# Revit family: LWplc_Latchwaysplc_BaluAndGuardSym_VersiRail_Ancillary
name_source: partatom
category: Railings
revit_build: Autodesk Revit 2013 (Build: 20121003_2115(x64)
units: mm (PartAtom-declared; Revit-internal decimal feet)

## types (5) — shared parameters
AssetType = Fixed
Description = Latchways ManSafe® for Roofing, using VersiRail
Diameter = 40 mm  [stored 0.131234 ft]
DurationUnit = year
GateMaterial = LWplc_Latchwaysplc_Aluminium_Polished
Height = 1100 mm
IfcExportAs = GUARDRAIL
IfcExportType = IfcRailing
IsExternal = Yes
ManufacturerName = Latchways plc
ManufacturerURL = www.latchways.com
Material = Handrails & Uprights: Aluminium
NBSDescription = Balustrade and guarding system
NBSReference = 25-25-10/110
NominalLength = 40 mm  [stored 0.131234 ft]
RailMaterial = LWplc_Latchwaysplc_Aluminium_Polished
SupportMaterial = LWplc_Latchwaysplc_Aluminium_Polished
URL = www.latchways.com
Uniclass2 = Ss_25_15_60_05
Version = 1
WarrantyDurationUnit = year
zero-valued in all types: Default Elevation

## per-type parameters (varying)
| type | 90DegreeCorner | AccessGate | BIMObjectName | ClosureEnd | HandRail | Model | ModelNumber | ModelReference | NominalHeight | NominalWidth | ProductInformation | Size | WallEndPiece |
| BalustradeAndGuardingSystem_VersiRailAncillary_90DegreeCorner_Latchwaysplc | Yes | No | LWplc_Latchwaysplc_BalustradeAndGuardingSystem_VersiRailAncillary_90DegreeCorner | No | No | 22061-00 | 22061-00 | VersiRail - Ancillary Items - 90 Degree Corner | 40 mm  [stored 0.131234 ft] | 160 mm  [stored 0.524934 ft] | www.latchways.com/BIM/Latchways_VersiRail_90DegreeCorner.pdf | 160 x 40 x 40 mm | No |
| BalustradeAndGuardingSystem_VersiRailAncillary_AccessGate_Latchwaysplc | No | Yes | LWplc_Latchwaysplc_BalustradeAndGuardingSystem_VersiRailAncillary_AccessGate | No | No | 22010-00 | 22010-00 | VersiRail - Ancillary Items - Access Gate | 510 mm  [stored 1.67323 ft] | 1160 mm  [stored 3.80577 ft] | www.latchways.com/BIM/Latchways_VersiRail_AccessGate.pdf | 1160 x 40 x 510 mm | No |
| BalustradeAndGuardingSystem_VersiRailAncillary_ClosureEnd_Latchwaysplc | No | No | LWplc_Latchwaysplc_BalustradeAndGuardingSystem_VersiRailAncillary_ClosureEnd | Yes | No | 22059-00 | 22059-00 | VersiRail - Ancillary Items - Closure End | 510 mm  [stored 1.67323 ft] | 160 mm  [stored 0.524934 ft] | www.latchways.com/BIM/Latchways_VersiRail_ClosureEndAssembly.pdf | 160 x 40 x 510 mm | No |
| BalustradeAndGuardingSystem_VersiRailAncillary_HandAndKneeRail_Latchwaysplc | No | No | LWplc_Latchwaysplc_BalustradeAndGuardingSystem_VersiRailAncillary_HandAndKneeRail
LWplc_Latchwaysplc_BalustradeAndGuardingSystem_VersiRailAncillary_Hand/KneeRail
LWplc_Latchwaysplc_BalustradeAndGuardingSystem_VersiRailAncillary_Hand/KneeRail | No | Yes | 22059-00 | 22013-00 | VersiRail - Ancillary Items - Hand And Knee Rail | 510 mm  [stored 1.67323 ft] | 160 mm  [stored 0.524934 ft] |  | 160 x 40 x 510 mm | No |
| BalustradeAndGuardingSystem_VersiRailAncillary_WallEndPiece_Latchwaysplc | No | No | LWplc_Latchwaysplc_BalustradeAndGuardingSystem_VersiRailAncillary_WallEndPiece | No | No | 22063-00 | 22063-00 | VersiRail - Ancillary Items - Wall End Piece | 40 mm  [stored 0.131234 ft] | 160 mm  [stored 0.524934 ft] | www.latchways.com/BIM/Latchways_VersiRail_WallEndFixingPlate.pdf | 160 x 40 x 40 mm | Yes |

note: column(s) folded — value = type name in every type: Name

note: [stored X ft] marks values corroborated as IEEE doubles in the binary element streams (Revit-internal decimal feet)

## geometry (parser evidence)
native form markers: Blend x2, Sweep x12
no freeform markers — native parametric forms only
